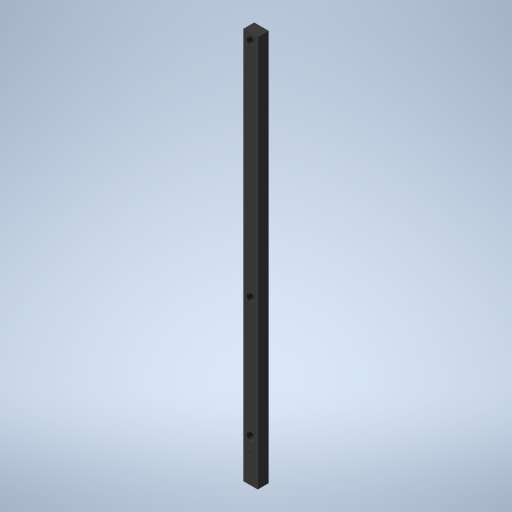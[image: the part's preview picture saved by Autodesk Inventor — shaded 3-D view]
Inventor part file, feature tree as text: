
AUTODESK INVENTOR PART (.ipt)
format: ipt  version: 2024 (Build 280153000, 153)  size: 272,384 bytes
history: native  units: in
note: dims shown in document units (in); Inventor stores cm internally (conversion verified against a paired STEP export)
features: hole x5, sketch x3, extrude x1
ambient origin geometry x8: Origin, YZ Plane, XZ Plane, XY Plane, X Axis, Y Axis, Z Axis, Center Point
bodies: Solid1 (feature_tree)
feature tree (9):
  extrude  "Extrusion1"  Depth=0.1875in
  sketch  "Sketch2"  dims[d2=0.138in d3=6.9363in d4=0.0in]
  hole  "Hole2"  [1 undecoded]
  hole  "Hole3"  [1 undecoded]
  hole  "Hole4"  [1 undecoded]
  hole  "Hole5"  [1 undecoded]
  hole  "Hole6"  [1 undecoded]
  sketch  "Sketch1"  dims[d0=0.25in d1=0.1875in]
  sketch  "Sketch3"  dims[d5=0.125in d6=0.138in d14=0.75in d15=0.138in d16=0.5in d17=0.04in d18=0.1495in d19=0.276in d20=0.279in d21=0.25in d22=0.5635in d23=1.0in d24=0.8108in d25=0.04in d26=0.75in d27=0.375in d28=0.25in d29=0.5635in d30=1.0in d31=0.8108in d32=0.1495in d33=0.75in d34=0.279in d35=0.25in d36=0.5635in d37=1.0in d38=0.8108in d39=0.104in d40=0.13in d41=0.5in d42=0.375in d43=0.25in d44=0.5635in d45=0.5in d46=0.0in d47=3.937in d48=0.138in d49=0.1495in d50=0.25in d51=0.279in d52=0.25in d53=0.5635in d54=0.25in d55=0.0in]
note: 5 required parameter values undecoded (feature->parameter linkage not recoverable at this tier; creation-order binding heuristic only, values carry confidence <= 0.55)
